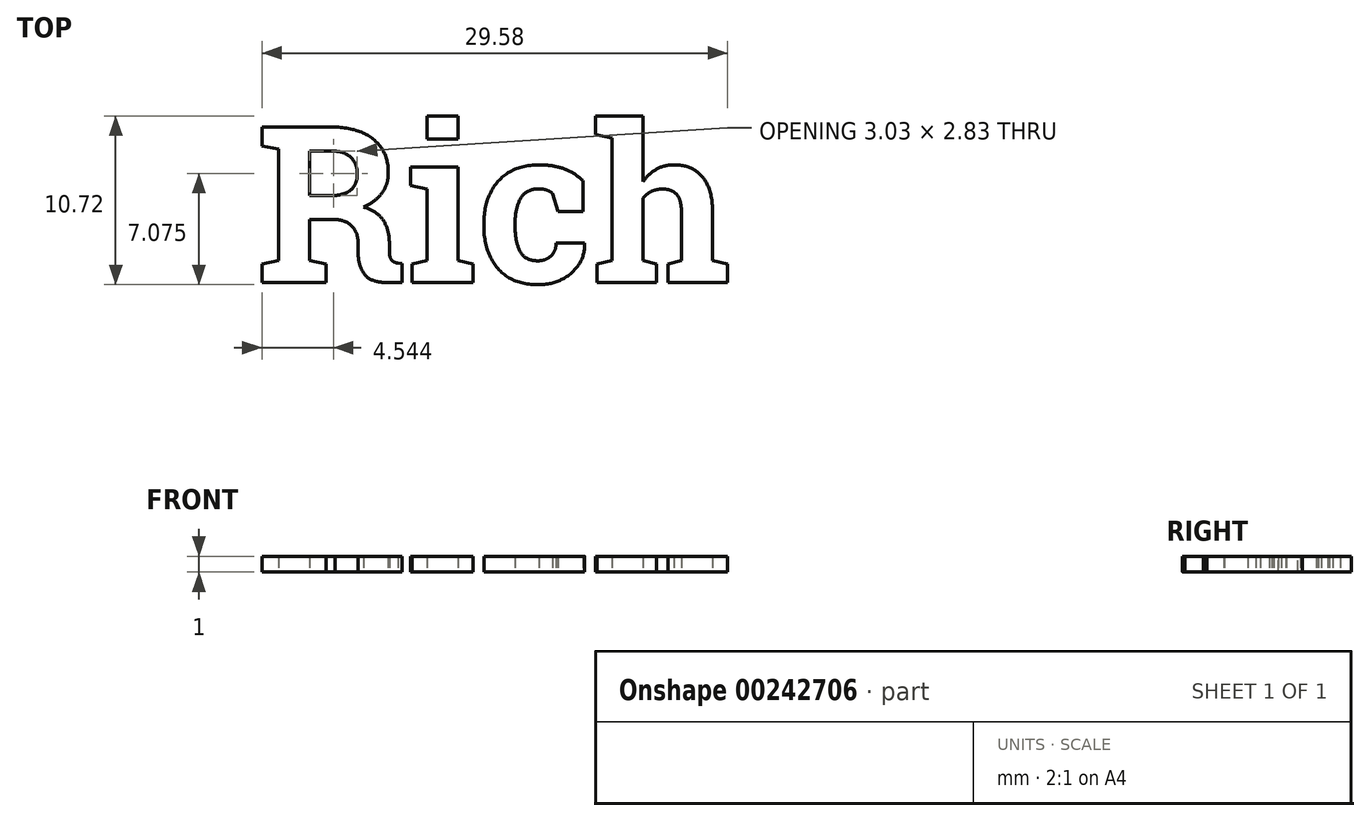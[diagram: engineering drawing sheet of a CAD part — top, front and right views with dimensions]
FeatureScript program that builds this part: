
annotation { "Feature Type Name" : "Feature", "Feature Type Description" : "" }
export const myFeature = defineFeature(function(context is Context, id is Id, definition is map)
    precondition{}
    {
        {
            var Q0;
            Q0=qCreatedBy(makeId("Top.planeOp"),FACE);
            var sketch = newSketch(context, id + "F0", { "sketchPlane" : qUnion([Q0])});
            skText(sketch, "E0", { "text": "Rich", "fontName": "RobotoSlab-Bold.ttf"});
            const initialGuessF0  = {"E0": [0, 0, 1, 0, 0.01]};
            skSetInitialGuess(sketch, initialGuessF0);
            skSolve(sketch);
        }
        {
            var Q0;
            Q0=makeQuery(id+"F0.imprint","IMPRINT",FACE,{"disambiguationData":[TD([[makeQuery(id+"F0.imprint","IMPRINT",EDGE,{"derivedFrom":sQuery(id+"F0.wireOp",EDGE,"E0.sketch_text.stroke-73")}),-1.0]])]});
            var Q1;
            Q1=makeQuery(id+"F0.imprint","IMPRINT",FACE,{"disambiguationData":[TD([[makeQuery(id+"F0.imprint","IMPRINT",EDGE,{"derivedFrom":sQuery(id+"F0.wireOp",EDGE,"E0.sketch_text.stroke-46")}),-1.0]])]});
            var Q2;
            Q2=makeQuery(id+"F0.imprint","IMPRINT",FACE,{"disambiguationData":[TD([[makeQuery(id+"F0.imprint","IMPRINT",EDGE,{"derivedFrom":sQuery(id+"F0.wireOp",EDGE,"E0.sketch_text.stroke-36")}),-1.0]])]});
            var Q3;
            Q3=makeQuery(id+"F0.imprint","IMPRINT",FACE,{"disambiguationData":[TD([[makeQuery(id+"F0.imprint","IMPRINT",EDGE,{"derivedFrom":sQuery(id+"F0.wireOp",EDGE,"E0.sketch_text.stroke-50")}),-1.0]])]});
            var Q4;
            Q4=makeQuery(id+"F0.imprint","IMPRINT",FACE,{"disambiguationData":[TD([[makeQuery(id+"F0.imprint","IMPRINT",EDGE,{"derivedFrom":sQuery(id+"F0.wireOp",EDGE,"E0.sketch_text.stroke-0")}),-1.0]])]});
            extrude(context, id + "F1", {"entities" : qUnion([Q0, Q1, Q2, Q3, Q4]), "depth" : 1 * mm});
        }
    });
